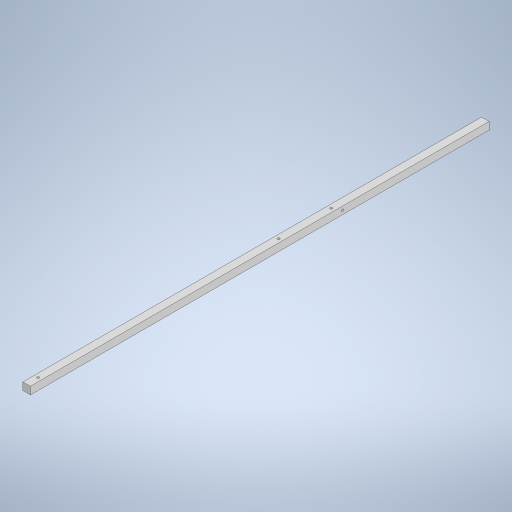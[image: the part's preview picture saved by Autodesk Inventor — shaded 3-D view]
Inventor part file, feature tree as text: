
AUTODESK INVENTOR PART (.ipt)
format: ipt  version: 2023 (Build 270158000, 158)  size: 253,952 bytes
history: native  units: mm
features: sketch x4, hole x3, other x1, extrude x1
ambient origin geometry x8: Origin, YZ Plane, XZ Plane, XY Plane, X Axis, Y Axis, Z Axis, Center Point
bodies: Body1 (feature_tree)
feature tree (9):
  other  "ソリッド1"
  extrude  "押し出し1"  Depth=10.0mm
  hole  "穴1"  [1 undecoded]
  hole  "穴2"  [1 undecoded]
  hole  "穴3"  [1 undecoded]
  sketch  "スケッチ1"
  sketch  "スケッチ2"
  sketch  "スケッチ3"
  sketch  "スケッチ4"
note: 3 required parameter values undecoded (feature->parameter linkage not recoverable at this tier; creation-order binding heuristic only, values carry confidence <= 0.55)
